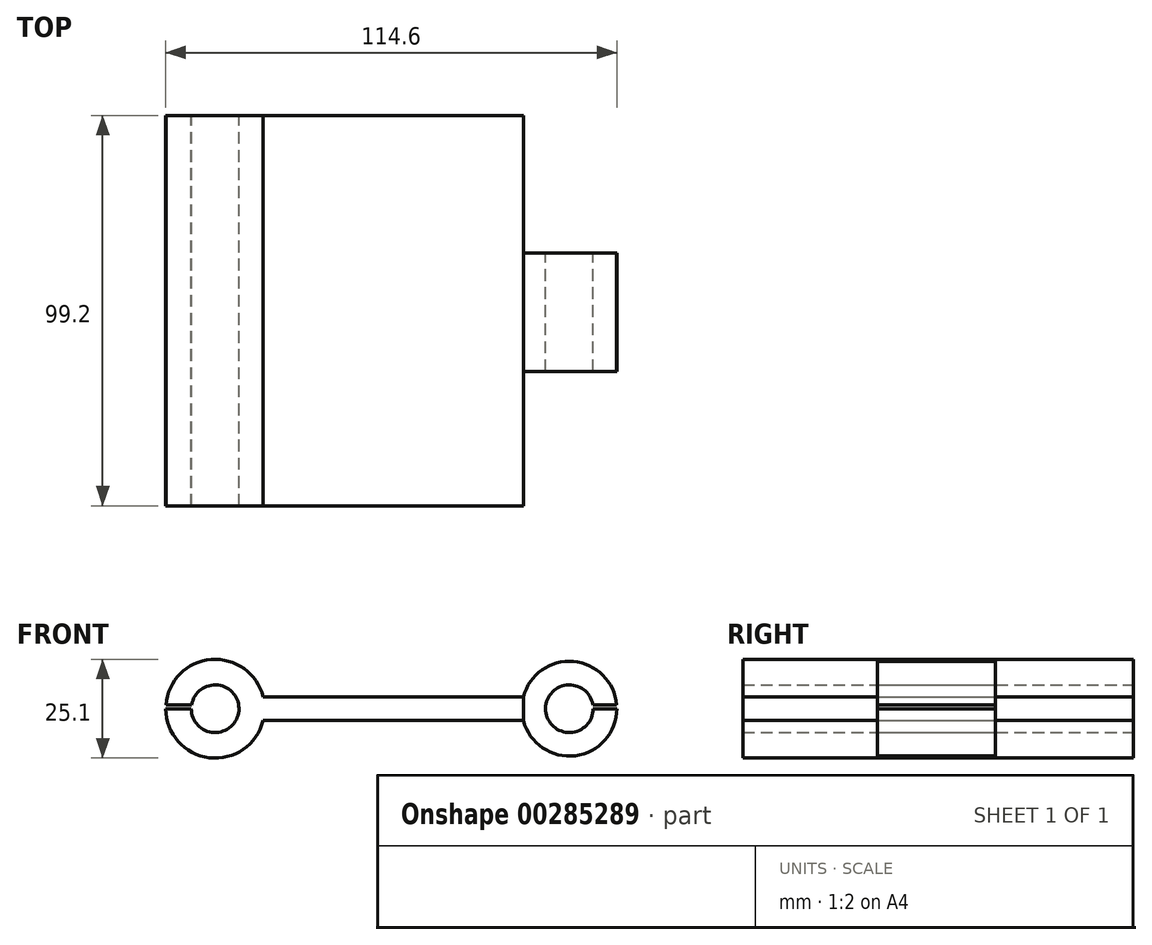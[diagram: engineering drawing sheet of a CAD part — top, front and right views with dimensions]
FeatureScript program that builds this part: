
annotation { "Feature Type Name" : "Feature", "Feature Type Description" : "" }
export const myFeature = defineFeature(function(context is Context, id is Id, definition is map)
    precondition{}
    {
        {
            var Q0;
            Q0=qCreatedBy(makeId("Front.planeOp"),FACE);
            var sketch = newSketch(context, id + "F0", { "sketchPlane" : qUnion([Q0])});
            skCircle(sketch, "E0", {"center": v(-49.94, 7.68) * mm, "radius": 6.05 * mm});
            skLineSegment(sketch, "E1", {"start": v(-49.94, 7.68) * mm, "end": v(40.06, 7.68) * mm});
            skCircle(sketch, "E2", {"center": v(40.06, 7.68) * mm, "radius": 6.05 * mm});
            skCircle(sketch, "E3.0", {"center": v(-49.94, 7.68) * mm, "radius": 12.55 * mm});
            skCircle(sketch, "E4.0", {"center": v(40.06, 7.68) * mm, "radius": 12.05 * mm});
            skLineSegment(sketch, "E5", {"start": v(-50.07, 10.68) * mm, "end": v(39.9, 10.68) * mm});
            skLineSegment(sketch, "E6", {"start": v(39.9, 10.68) * mm, "end": v(39.9, 4.69) * mm});
            skLineSegment(sketch, "E7", {"start": v(39.9, 4.69) * mm, "end": v(-49.8, 4.69) * mm});
            skLineSegment(sketch, "E8", {"start": v(-49.8, 4.69) * mm, "end": v(-50.07, 10.68) * mm});
            skLineSegment(sketch, "E9", {"start": v(-49.94, 7.68) * mm, "end": v(-49.8, 4.69) * mm});
            skLineSegment(sketch, "E10", {"start": v(-49.94, 7.68) * mm, "end": v(-62.5, 7.68) * mm});
            skLineSegment(sketch, "E11", {"start": v(-62.5, 7.68) * mm, "end": v(-62.5, 8.68) * mm});
            skLineSegment(sketch, "E12", {"start": v(-62.5, 8.68) * mm, "end": v(-49.94, 8.68) * mm});
            skLineSegment(sketch, "E13", {"start": v(-49.94, 8.68) * mm, "end": v(52.07, 8.68) * mm});
            skLineSegment(sketch, "E14", {"start": v(40.06, 7.68) * mm, "end": v(52.1, 7.68) * mm});
            skSolve(sketch);
        }
        {
            var Q0;
            {var subQ0=sQuery(id+"F0.wireOp",EDGE,"E5");var subQ1=sQuery(id+"F0.wireOp",EDGE,"E0");var subQ2=makeQuery(id+"F0.imprint","INTERSECT",VERTEX,{"derivedFrom":[subQ1,subQ0]});Q0=makeQuery(id+"F0.imprint","IMPRINT",FACE,{"disambiguationData":[TD([[makeQuery(id+"F0.imprint","IMPRINT",EDGE,{"disambiguationData":[TD([[subQ2,-1.0]])],"derivedFrom":subQ1}),-1.0]])]});}
            var Q1;
            {var subQ0=sQuery(id+"F0.wireOp",EDGE,"E10");var subQ1=sQuery(id+"F0.wireOp",EDGE,"E0");var subQ2=makeQuery(id+"F0.imprint","INTERSECT",VERTEX,{"derivedFrom":[subQ1,subQ0]});Q1=makeQuery(id+"F0.imprint","IMPRINT",FACE,{"disambiguationData":[TD([[makeQuery(id+"F0.imprint","IMPRINT",EDGE,{"disambiguationData":[TD([[subQ2,-1.0]])],"derivedFrom":subQ1}),-1.0]])]});}
            var Q2;
            {var subQ0=sQuery(id+"F0.wireOp",EDGE,"E3.0");var subQ1=sQuery(id+"F0.wireOp",EDGE,"E1");var subQ2=makeQuery(id+"F0.imprint","INTERSECT",VERTEX,{"derivedFrom":[subQ1,subQ0]});Q2=makeQuery(id+"F0.imprint","IMPRINT",FACE,{"disambiguationData":[TD([[makeQuery(id+"F0.imprint","IMPRINT",EDGE,{"disambiguationData":[TD([[subQ2,-1.0]])],"derivedFrom":subQ1}),-1.0]])]});}
            var Q3;
            {var subQ0=sQuery(id+"F0.wireOp",EDGE,"E13");var subQ1=sQuery(id+"F0.wireOp",EDGE,"E2");var subQ2=makeQuery(id+"F0.imprint","INTERSECT",VERTEX,{"disambiguationData":[OD(0.0)],"derivedFrom":[subQ1,subQ0]});Q3=makeQuery(id+"F0.imprint","IMPRINT",FACE,{"disambiguationData":[TD([[makeQuery(id+"F0.imprint","IMPRINT",EDGE,{"disambiguationData":[TD([[subQ2,-1.0]])],"derivedFrom":subQ1}),-1.0]])]});}
            var Q4;
            {var subQ0=sQuery(id+"F0.wireOp",EDGE,"E14");var subQ1=sQuery(id+"F0.wireOp",EDGE,"E2");var subQ2=makeQuery(id+"F0.imprint","INTERSECT",VERTEX,{"derivedFrom":[subQ1,subQ0]});Q4=makeQuery(id+"F0.imprint","IMPRINT",FACE,{"disambiguationData":[TD([[makeQuery(id+"F0.imprint","IMPRINT",EDGE,{"disambiguationData":[TD([[subQ2,1.0]])],"derivedFrom":subQ1}),-1.0]])]});}
            var Q5;
            {var subQ0=sQuery(id+"F0.wireOp",EDGE,"E5");var subQ1=sQuery(id+"F0.wireOp",EDGE,"E3.0");var subQ2=makeQuery(id+"F0.imprint","INTERSECT",VERTEX,{"derivedFrom":[subQ1,subQ0]});Q5=makeQuery(id+"F0.imprint","IMPRINT",FACE,{"disambiguationData":[TD([[makeQuery(id+"F0.imprint","IMPRINT",EDGE,{"disambiguationData":[TD([[subQ2,1.0]])],"derivedFrom":subQ1}),-1.0]])]});}
            var Q6;
            {var subQ0=sQuery(id+"F0.wireOp",EDGE,"E13");var subQ1=sQuery(id+"F0.wireOp",EDGE,"E0");var subQ2=makeQuery(id+"F0.imprint","INTERSECT",VERTEX,{"derivedFrom":[subQ1,subQ0]});Q6=makeQuery(id+"F0.imprint","IMPRINT",FACE,{"disambiguationData":[TD([[makeQuery(id+"F0.imprint","IMPRINT",EDGE,{"disambiguationData":[TD([[subQ2,-1.0]])],"derivedFrom":subQ1}),-1.0]])]});}
            var Q7;
            {var subQ0=sQuery(id+"F0.wireOp",EDGE,"E1");var subQ1=sQuery(id+"F0.wireOp",EDGE,"E0");var subQ2=makeQuery(id+"F0.imprint","INTERSECT",VERTEX,{"derivedFrom":[subQ1,subQ0]});Q7=makeQuery(id+"F0.imprint","IMPRINT",FACE,{"disambiguationData":[TD([[makeQuery(id+"F0.imprint","IMPRINT",EDGE,{"disambiguationData":[TD([[subQ2,1.0]])],"derivedFrom":subQ1}),-1.0]])]});}
            var Q8;
            {var subQ0=sQuery(id+"F0.wireOp",EDGE,"E4.0");var subQ1=sQuery(id+"F0.wireOp",EDGE,"E1");var subQ2=makeQuery(id+"F0.imprint","INTERSECT",VERTEX,{"derivedFrom":[subQ1,subQ0]});Q8=makeQuery(id+"F0.imprint","IMPRINT",FACE,{"disambiguationData":[TD([[makeQuery(id+"F0.imprint","IMPRINT",EDGE,{"disambiguationData":[TD([[subQ2,-1.0]])],"derivedFrom":subQ1}),-1.0]])]});}
            var Q9;
            {var subQ0=sQuery(id+"F0.wireOp",EDGE,"E5");var subQ1=sQuery(id+"F0.wireOp",EDGE,"E2");var subQ2=makeQuery(id+"F0.imprint","INTERSECT",VERTEX,{"derivedFrom":[subQ1,subQ0]});Q9=makeQuery(id+"F0.imprint","IMPRINT",FACE,{"disambiguationData":[TD([[makeQuery(id+"F0.imprint","IMPRINT",EDGE,{"disambiguationData":[TD([[subQ2,-1.0]])],"derivedFrom":subQ1}),-1.0]])]});}
            var Q10;
            {var subQ0=sQuery(id+"F0.wireOp",EDGE,"E3.0");var subQ1=sQuery(id+"F0.wireOp",EDGE,"E1");var subQ2=makeQuery(id+"F0.imprint","INTERSECT",VERTEX,{"derivedFrom":[subQ1,subQ0]});Q10=makeQuery(id+"F0.imprint","IMPRINT",FACE,{"disambiguationData":[TD([[makeQuery(id+"F0.imprint","IMPRINT",EDGE,{"disambiguationData":[TD([[subQ2,-1.0]])],"derivedFrom":subQ1}),1.0]])]});}
            var Q11;
            {var subQ0=sQuery(id+"F0.wireOp",EDGE,"E13");var subQ1=sQuery(id+"F0.wireOp",EDGE,"E0");var subQ2=makeQuery(id+"F0.imprint","INTERSECT",VERTEX,{"derivedFrom":[subQ1,subQ0]});Q11=makeQuery(id+"F0.imprint","IMPRINT",FACE,{"disambiguationData":[TD([[makeQuery(id+"F0.imprint","IMPRINT",EDGE,{"disambiguationData":[TD([[subQ2,1.0]])],"derivedFrom":subQ1}),-1.0]])]});}
            var Q12;
            {var subQ0=sQuery(id+"F0.wireOp",EDGE,"E4.0");var subQ1=sQuery(id+"F0.wireOp",EDGE,"E1");var subQ2=makeQuery(id+"F0.imprint","INTERSECT",VERTEX,{"derivedFrom":[subQ1,subQ0]});Q12=makeQuery(id+"F0.imprint","IMPRINT",FACE,{"disambiguationData":[TD([[makeQuery(id+"F0.imprint","IMPRINT",EDGE,{"disambiguationData":[TD([[subQ2,-1.0]])],"derivedFrom":subQ1}),1.0]])]});}
            extrude(context, id + "F1", {"entities" : qUnion([Q0, Q1, Q2, Q3, Q4, Q5, Q6, Q7, Q8, Q9, Q10, Q11, Q12]), "depth" : 87.2 * mm});
        }
        {
            var Q0;
            Q0=makeQuery(id+"F1.opExtrude","CAP_FACE",FACE,{"disambiguationData":[OSD([sQuery(id+"F0.wireOp",EDGE,"E0"),sQuery(id+"F0.wireOp",EDGE,"E2"),sQuery(id+"F0.wireOp",EDGE,"E3.0"),sQuery(id+"F0.wireOp",EDGE,"E4.0"),sQuery(id+"F0.wireOp",EDGE,"E5"),sQuery(id+"F0.wireOp",EDGE,"E7"),sQuery(id+"F0.wireOp",EDGE,"E10"),sQuery(id+"F0.wireOp",EDGE,"E12"),sQuery(id+"F0.wireOp",EDGE,"E13"),sQuery(id+"F0.wireOp",EDGE,"E14")])],"isStart":false});
            extrude(context, id + "F2", {"entities" : qUnion([Q0]), "operationType" : NewBodyOperationType.ADD, "depth" : 12 * mm});
        }
        {
            var Q0;
            {var subQ0=sQuery(id+"F0.wireOp",EDGE,"E5");Q0=makeQuery(id+"F2.boolean.opBoolean","MERGE",FACE,{"derivedFrom":[makeQuery(id+"F1.opExtrude","SWEPT_FACE",FACE,{"disambiguationData":[OSD([subQ0])]}),makeQuery(id+"F2.opExtrude","SWEPT_FACE",FACE,{"disambiguationData":[OSD([subQ0])]})]});}
            cPlane(context, id + "F3", {"entities" : qUnion([Q0]), "cplaneType" : CPlaneType.OFFSET, "offset" : 25 * mm, "width" : 150 * mm, "height" : 150 * mm});
        }
        {
            var Q0;
            Q0=qCreatedBy(id+"F3.planeOp",FACE);
            var sketch = newSketch(context, id + "F4", { "sketchPlane" : qUnion([Q0])});
            skLineSegment(sketch, "E15.bottom", {"start": v(-37.75, -99.2) * mm, "end": v(28.39, -99.2) * mm});
            skLineSegment(sketch, "E15.top", {"start": v(-37.75, 0) * mm, "end": v(28.39, 0) * mm});
            skLineSegment(sketch, "E15.left", {"start": v(-37.75, -99.2) * mm, "end": v(-37.75, 0) * mm});
            skLineSegment(sketch, "E16.bottom", {"start": v(-37.75, -99.2) * mm, "end": v(-74.5, -99.2) * mm});
            skLineSegment(sketch, "E16.top", {"start": v(-37.75, -69.2) * mm, "end": v(-74.5, -69.2) * mm});
            skLineSegment(sketch, "E16.left", {"start": v(-37.75, -99.2) * mm, "end": v(-37.75, -69.2) * mm});
            skLineSegment(sketch, "E16.right", {"start": v(-74.5, -99.2) * mm, "end": v(-74.5, -69.2) * mm});
            skLineSegment(sketch, "E17.bottom", {"start": v(-37.75, 0) * mm, "end": v(-74.31, 0) * mm});
            skLineSegment(sketch, "E17.top", {"start": v(-37.75, -30) * mm, "end": v(-74.31, -30) * mm});
            skLineSegment(sketch, "E17.left", {"start": v(-37.75, 0) * mm, "end": v(-37.75, -30) * mm});
            skLineSegment(sketch, "E17.right", {"start": v(-74.31, 0) * mm, "end": v(-74.31, -30) * mm});
            skLineSegment(sketch, "E18.bottom", {"start": v(-37.75, -69.2) * mm, "end": v(-74.31, -69.2) * mm});
            skLineSegment(sketch, "E18.left", {"start": v(-37.75, -69.2) * mm, "end": v(-37.75, -30) * mm});
            skLineSegment(sketch, "E18.right", {"start": v(-74.31, -69.2) * mm, "end": v(-74.31, -30) * mm});
            skLineSegment(sketch, "E19", {"start": v(28.39, -50.03) * mm, "end": v(24.92, -50.03) * mm});
            skPoint(sketch, "E19.endSnap0", {"position": v(28.39, -50.03) * mm});
            skLineSegment(sketch, "E20", {"start": v(28.39, -50.03) * mm, "end": v(28.39, -35.03) * mm});
            skLineSegment(sketch, "E21", {"start": v(28.39, -50.03) * mm, "end": v(28.39, -65.03) * mm});
            skLineSegment(sketch, "E22", {"start": v(28.39, -65.03) * mm, "end": v(66.48, -65.03) * mm});
            skLineSegment(sketch, "E23", {"start": v(66.48, -65.03) * mm, "end": v(66.48, -35.03) * mm});
            skLineSegment(sketch, "E24", {"start": v(66.48, -35.03) * mm, "end": v(28.39, -35.03) * mm});
            skLineSegment(sketch, "E25.bottom", {"start": v(28.39, -65.03) * mm, "end": v(88.27, -65.03) * mm});
            skLineSegment(sketch, "E25.top", {"start": v(28.39, -157.01) * mm, "end": v(88.27, -157.01) * mm});
            skLineSegment(sketch, "E25.left", {"start": v(28.39, -65.03) * mm, "end": v(28.39, -157.01) * mm});
            skLineSegment(sketch, "E25.right", {"start": v(88.27, -65.03) * mm, "end": v(88.27, -157.01) * mm});
            skLineSegment(sketch, "E26.bottom", {"start": v(28.39, -35.03) * mm, "end": v(79.68, -35.03) * mm});
            skLineSegment(sketch, "E26.top", {"start": v(28.39, 31.78) * mm, "end": v(79.68, 31.78) * mm});
            skLineSegment(sketch, "E26.left", {"start": v(28.39, -35.03) * mm, "end": v(28.39, 31.78) * mm});
            skLineSegment(sketch, "E26.right", {"start": v(79.68, -35.03) * mm, "end": v(79.68, 31.78) * mm});
            skSolve(sketch);
        }
        {
            var Q0;
            {var subQ4=sQuery(id+"F4.wireOp",EDGE,"E25.top");Q0=makeQuery(id+"F4.imprint","IMPRINT",FACE,{"disambiguationData":[TD([[makeQuery(id+"F4.imprint","IMPRINT",EDGE,{"derivedFrom":subQ4}),1.0]])]});}
            var Q1;
            {var subQ4=sQuery(id+"F4.wireOp",EDGE,"E26.top");Q1=makeQuery(id+"F4.imprint","IMPRINT",FACE,{"disambiguationData":[TD([[makeQuery(id+"F4.imprint","IMPRINT",EDGE,{"derivedFrom":subQ4}),-1.0]])]});}
            var Q2;
            Q2=makeQuery(id+"F4.imprint","IMPRINT",FACE,{"disambiguationData":[TD([[makeQuery(id+"F4.imprint","IMPRINT",EDGE,{"derivedFrom":sQuery(id+"F4.wireOp",EDGE,"E18.bottom")}),-1.0]])]});
            extrude(context, id + "F5", {"entities" : qUnion([Q0, Q1, Q2]), "operationType" : NewBodyOperationType.REMOVE, "oppositeDirection" : true, "depth" : 112.6 * mm});
        }
    });
